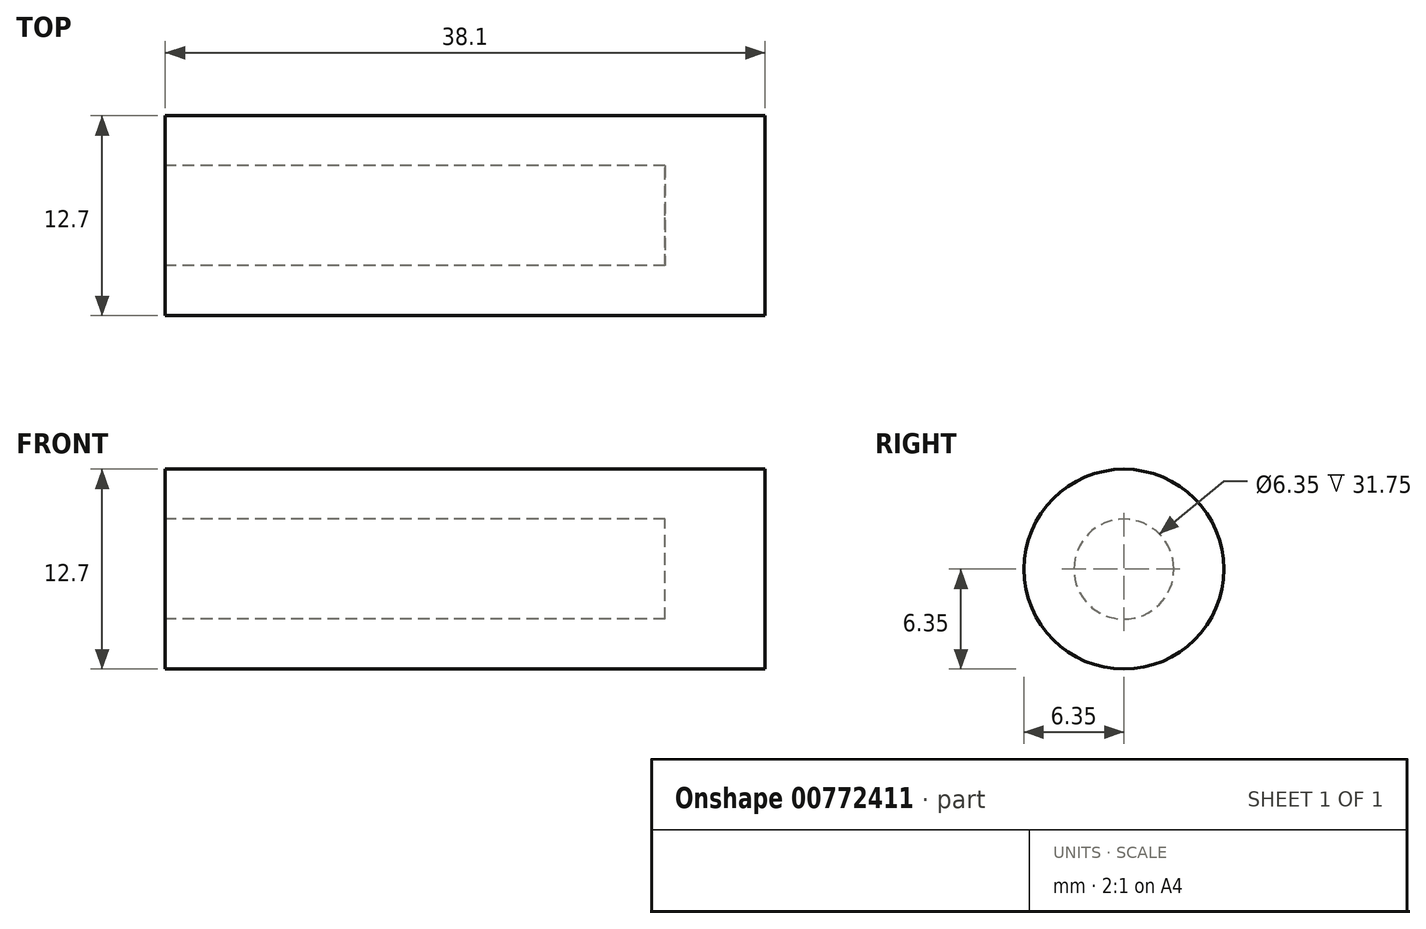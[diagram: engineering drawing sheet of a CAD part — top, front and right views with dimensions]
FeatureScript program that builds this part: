
annotation { "Feature Type Name" : "Feature", "Feature Type Description" : "" }
export const myFeature = defineFeature(function(context is Context, id is Id, definition is map)
    precondition{}
    {
        {
            var Q0;
            Q0=qCreatedBy(makeId("Right.planeOp"),FACE);
            var sketch = newSketch(context, id + "F0", { "sketchPlane" : qUnion([Q0])});
            skCircle(sketch, "E0", {"center": v(0, 0) * mm, "radius": 6.35 * mm});
            skCircle(sketch, "E1", {"center": v(0, 0) * mm, "radius": 3.18 * mm});
            skSolve(sketch);
        }
        {
            var Q0;
            Q0=makeQuery(id+"F0.imprint","IMPRINT",FACE,{"disambiguationData":[TD([[makeQuery(id+"F0.imprint","IMPRINT",EDGE,{"derivedFrom":sQuery(id+"F0.wireOp",EDGE,"E0")}),1.0]])]});
            extrude(context, id + "F1", {"entities" : qUnion([Q0]), "depth" : 31.75 * mm, "offsetDistance" : 25.4 * mm});
        }
        {
            var Q0;
            Q0=makeQuery(id+"F1.opExtrude","CAP_FACE",FACE,{"disambiguationData":[OSD([sQuery(id+"F0.wireOp",EDGE,"E0"),sQuery(id+"F0.wireOp",EDGE,"E1")])],"isStart":false});
            var sketch = newSketch(context, id + "F2", { "sketchPlane" : qUnion([Q0])});
            skCircle(sketch, "E2.0", {"center": v(0, 0) * mm, "radius": 6.35 * mm});
            skSolve(sketch);
        }
        {
            var Q0;
            Q0 = qSketchRegion(id + "F2", true);
            var Q1;
            Q1=sQuery(id+"F2.wireOp",EDGE,"E2.0");
            extrude(context, id + "F3", {"entities" : qUnion([Q0]), "operationType" : NewBodyOperationType.ADD, "surfaceEntities" : qUnion([Q1]), "depth" : 6.35 * mm, "offsetDistance" : 25.4 * mm});
        }
    });
